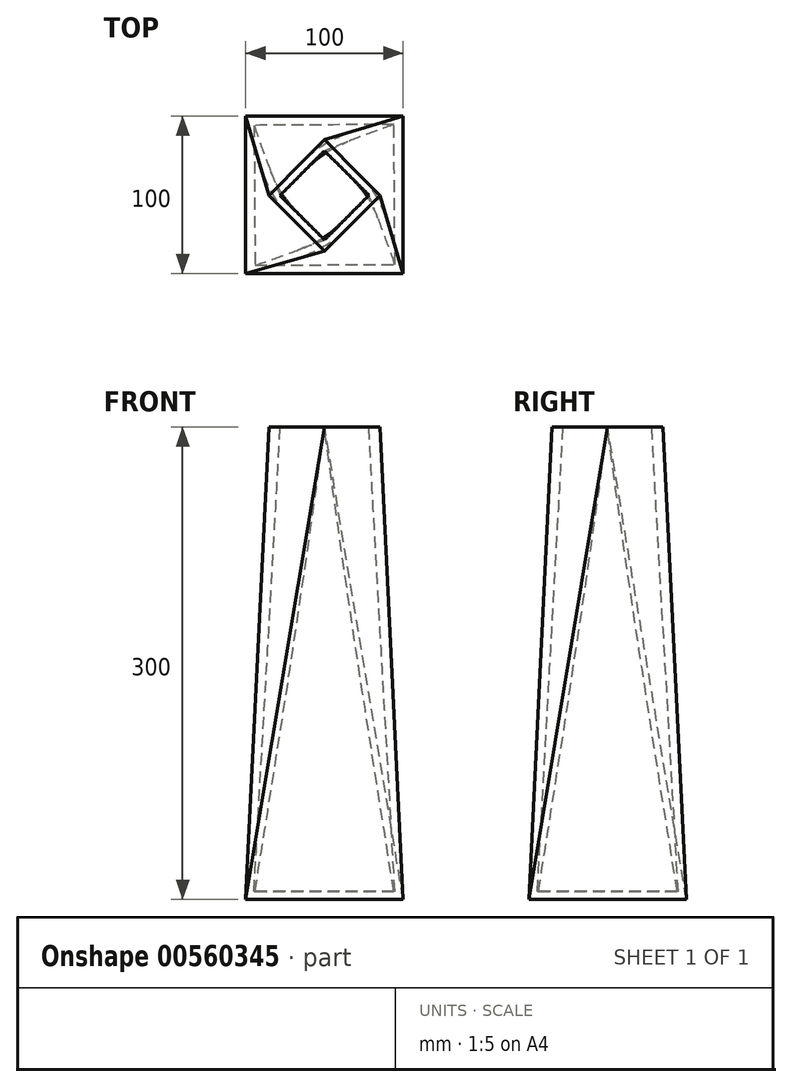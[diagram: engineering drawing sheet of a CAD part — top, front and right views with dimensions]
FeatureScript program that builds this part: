
annotation { "Feature Type Name" : "Feature", "Feature Type Description" : "" }
export const myFeature = defineFeature(function(context is Context, id is Id, definition is map)
    precondition{}
    {
        {
            var Q0;
            Q0=qCreatedBy(makeId("Top.planeOp"),FACE);
            var sketch = newSketch(context, id + "F0", { "sketchPlane" : qUnion([Q0])});
            skLineSegment(sketch, "E0.bottom", {"start": v(50, 50) * mm, "end": v(-50, 50) * mm});
            skLineSegment(sketch, "E0.top", {"start": v(50, -50) * mm, "end": v(-50, -50) * mm});
            skLineSegment(sketch, "E0.left", {"start": v(50, 50) * mm, "end": v(50, -50) * mm});
            skLineSegment(sketch, "E0.right", {"start": v(-50, 50) * mm, "end": v(-50, -50) * mm});
            skPoint(sketch, "E0.middle", {"position": v(0, 0) * mm});
            skSolve(sketch);
        }
        {
            var Q0;
            Q0=qCreatedBy(makeId("Top.planeOp"),FACE);
            cPlane(context, id + "F1", {"entities" : qUnion([Q0]), "cplaneType" : CPlaneType.OFFSET, "offset" : 300 * mm, "width" : 150 * mm, "height" : 150 * mm});
        }
        {
            var Q0;
            Q0=qCreatedBy(id+"F1.planeOp",FACE);
            var sketch = newSketch(context, id + "F2", { "sketchPlane" : qUnion([Q0])});
            skLineSegment(sketch, "E1.bottom", {"start": v(35.36, -0.32) * mm, "end": v(0, 35.03) * mm});
            skLineSegment(sketch, "E1.top", {"start": v(0, -35.68) * mm, "end": v(-35.36, -0.32) * mm});
            skLineSegment(sketch, "E1.left", {"start": v(35.36, -0.32) * mm, "end": v(0, -35.68) * mm});
            skLineSegment(sketch, "E1.right", {"start": v(0, 35.03) * mm, "end": v(-35.36, -0.32) * mm});
            skPoint(sketch, "E1.middle", {"position": v(0, 0) * mm});
            skSolve(sketch);
        }
        {
            var Q0;
            Q0=makeQuery(id+"F0.imprint","IMPRINT",FACE,{"disambiguationData":[TD([[makeQuery(id+"F0.imprint","IMPRINT",EDGE,{"derivedFrom":sQuery(id+"F0.wireOp",EDGE,"E0.bottom")}),1.0]])]});
            var Q1;
            Q1=makeQuery(id+"F2.imprint","IMPRINT",FACE,{"disambiguationData":[TD([[makeQuery(id+"F2.imprint","IMPRINT",EDGE,{"derivedFrom":sQuery(id+"F2.wireOp",EDGE,"E1.bottom")}),1.0]])]});
            var Q2;
            Q2=sQuery(id+"F2.wireOp",VERTEX,"E1.right.start");
            var Q3;
            Q3=sQuery(id+"F0.wireOp",VERTEX,"E0.top.start");
            loft(context, id + "F3", {"sheetProfilesArray" : [{ "sheetProfileEntities" : qUnion([Q0]) }, { "sheetProfileEntities" : qUnion([Q1]) }], "connections" : [{ "connectionEntities" : qUnion([Q2, Q3]), "connectionEdgeQueries" : qUnion([]), "connectionEdgeParameters" : [] }]});
        }
        {
            var Q0;
            Q0=makeQuery(id+"F3.opLoft","CAP_FACE",FACE,{"disambiguationData":[OSD([makeQuery(id+"F2.imprint","IMPRINT",FACE,{"disambiguationData":[TD([[makeQuery(id+"F2.imprint","IMPRINT",EDGE,{"derivedFrom":sQuery(id+"F2.wireOp",EDGE,"E1.bottom")}),1.0]])]})])],"isStart":true});
            shell(context, id + "F4", {"entities" : qUnion([Q0]), "thickness" : 5 * mm});
        }
    });
